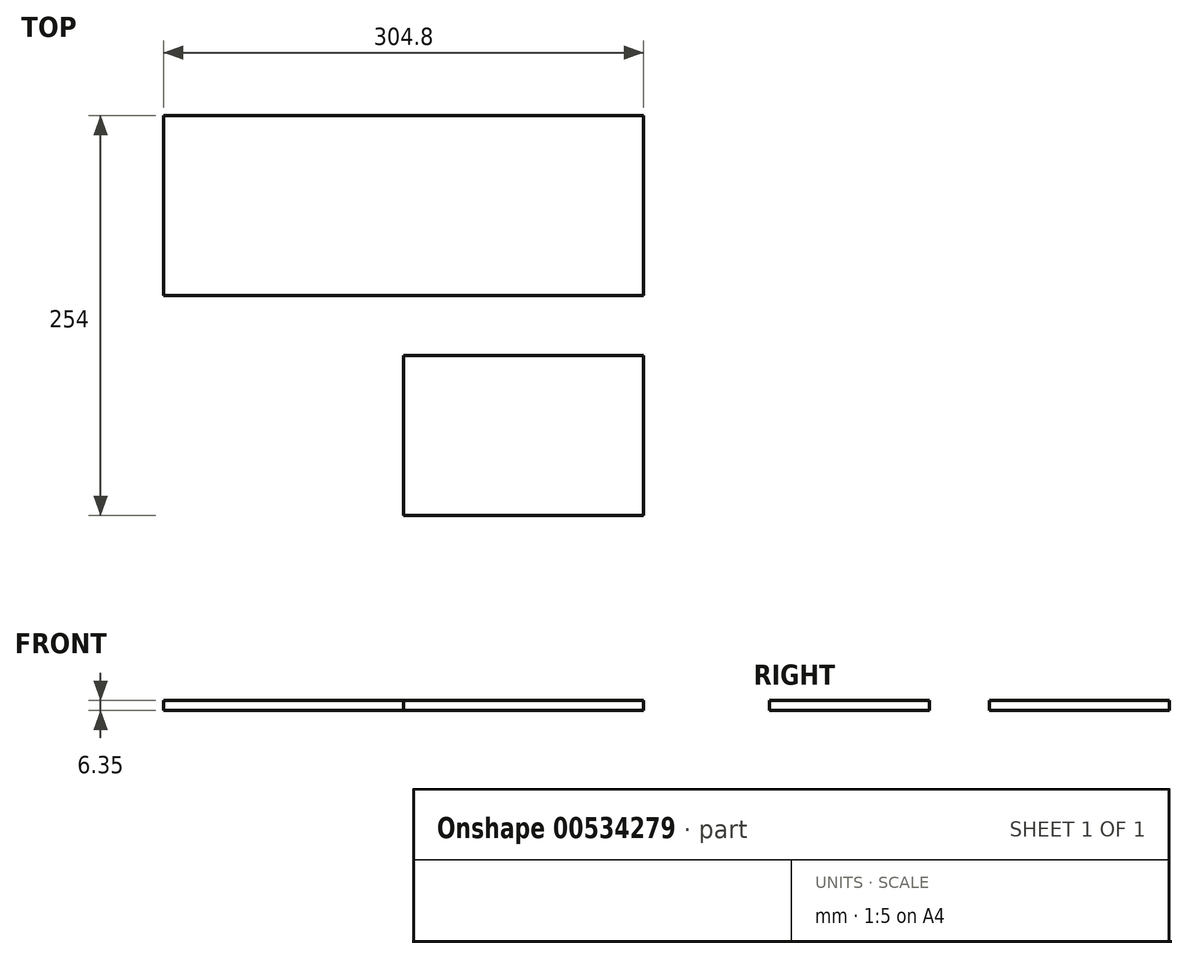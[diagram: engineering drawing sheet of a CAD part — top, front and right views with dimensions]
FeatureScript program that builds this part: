
annotation { "Feature Type Name" : "Feature", "Feature Type Description" : "" }
export const myFeature = defineFeature(function(context is Context, id is Id, definition is map)
    precondition{}
    {
        {
            var Q0;
            Q0=qCreatedBy(makeId("Top.planeOp"),FACE);
            var sketch = newSketch(context, id + "F0", { "sketchPlane" : qUnion([Q0])});
            skLineSegment(sketch, "E0.bottom", {"start": v(-124.66, 142.25) * mm, "end": v(180.14, 142.25) * mm});
            skLineSegment(sketch, "E0.top", {"start": v(-124.66, -111.75) * mm, "end": v(180.14, -111.75) * mm});
            skLineSegment(sketch, "E0.left", {"start": v(-124.66, 142.25) * mm, "end": v(-124.66, -111.75) * mm});
            skLineSegment(sketch, "E0.right", {"start": v(180.14, 142.25) * mm, "end": v(180.14, -111.75) * mm});
            skLineSegment(sketch, "E1.bottom", {"start": v(180.14, -111.75) * mm, "end": v(27.74, -111.75) * mm});
            skLineSegment(sketch, "E1.top", {"start": v(180.14, -10.15) * mm, "end": v(27.74, -10.15) * mm});
            skLineSegment(sketch, "E1.left", {"start": v(180.14, -111.75) * mm, "end": v(180.14, -10.15) * mm});
            skLineSegment(sketch, "E1.right", {"start": v(27.74, -111.75) * mm, "end": v(27.74, -10.15) * mm});
            skLineSegment(sketch, "E2", {"start": v(-124.66, 27.95) * mm, "end": v(180.14, 27.95) * mm});
            skLineSegment(sketch, "E3", {"start": v(-48.46, 142.25) * mm, "end": v(-48.46, 27.95) * mm});
            skLineSegment(sketch, "E4", {"start": v(27.74, 142.16) * mm, "end": v(27.74, 27.95) * mm});
            skPoint(sketch, "E4.startSnap0", {"position": v(27.74, 142.25) * mm});
            skLineSegment(sketch, "E5", {"start": v(103.94, 142.25) * mm, "end": v(103.94, 27.95) * mm});
            skSolve(sketch);
        }
        {
            var Q0;
            {var subQ3=sQuery(id+"F0.wireOp",EDGE,"E3");Q0=makeQuery(id+"F0.imprint","IMPRINT",FACE,{"disambiguationData":[TD([[makeQuery(id+"F0.imprint","IMPRINT",EDGE,{"derivedFrom":subQ3}),-1.0]])]});}
            var Q1;
            {var subQ3=sQuery(id+"F0.wireOp",EDGE,"E3");Q1=makeQuery(id+"F0.imprint","IMPRINT",FACE,{"disambiguationData":[TD([[makeQuery(id+"F0.imprint","IMPRINT",EDGE,{"derivedFrom":subQ3}),1.0]])]});}
            var Q2;
            {var subQ3=sQuery(id+"F0.wireOp",EDGE,"E5");Q2=makeQuery(id+"F0.imprint","IMPRINT",FACE,{"disambiguationData":[TD([[makeQuery(id+"F0.imprint","IMPRINT",EDGE,{"derivedFrom":subQ3}),1.0]])]});}
            var Q3;
            {var subQ5=sQuery(id+"F0.wireOp",EDGE,"E0.top");Q3=makeQuery(id+"F0.imprint","IMPRINT",FACE,{"disambiguationData":[TD([[makeQuery(id+"F0.imprint","IMPRINT",EDGE,{"derivedFrom":subQ5}),1.0]])]});}
            var Q4;
            Q4=makeQuery(id+"F0.imprint","IMPRINT",FACE,{"disambiguationData":[TD([[makeQuery(id+"F0.imprint","IMPRINT",EDGE,{"derivedFrom":sQuery(id+"F0.wireOp",EDGE,"E1.bottom")}),-1.0]])]});
            extrude(context, id + "F1", {"entities" : qUnion([Q0, Q1, Q2, Q3, Q4]), "oppositeDirection" : true, "depth" : 6.35 * mm, "offsetDistance" : 25.4 * mm});
        }
    });
